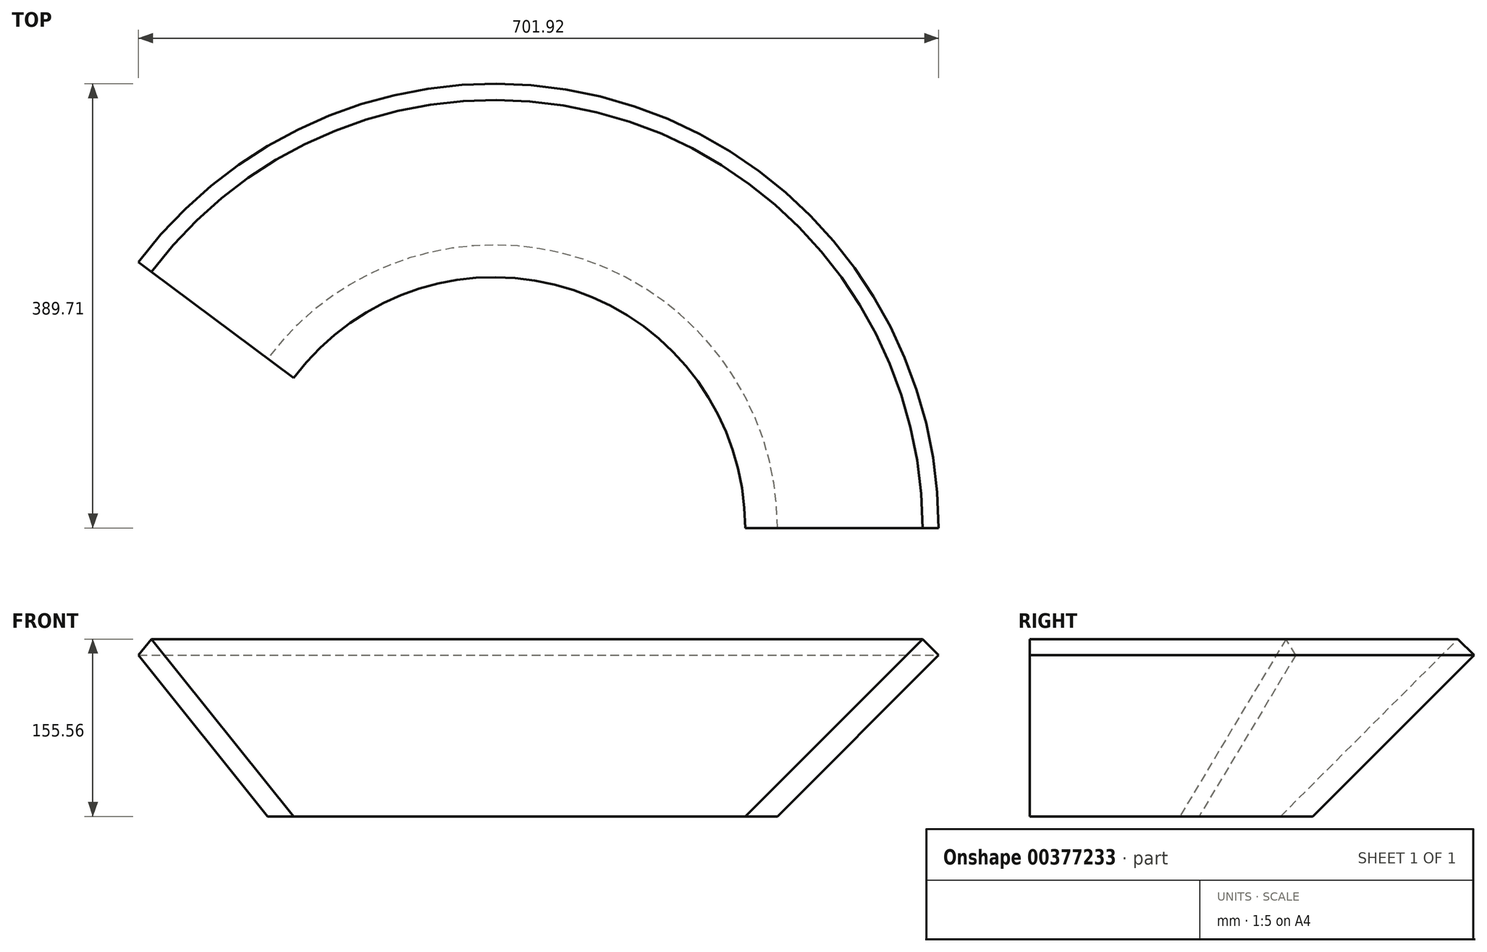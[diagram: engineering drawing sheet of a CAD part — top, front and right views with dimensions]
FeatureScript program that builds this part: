
annotation { "Feature Type Name" : "Feature", "Feature Type Description" : "" }
export const myFeature = defineFeature(function(context is Context, id is Id, definition is map)
    precondition{}
    {
        {
            var Q0;
            Q0=qCreatedBy(makeId("Front.planeOp"),FACE);
            var sketch = newSketch(context, id + "F0", { "sketchPlane" : qUnion([Q0])});
            skLineSegment(sketch, "E0", {"start": v(38.97, 15.56) * mm, "end": v(37.56, 16.97) * mm});
            skLineSegment(sketch, "E1", {"start": v(0, 22) * mm, "end": v(0, 0) * mm, "construction": true});
            skLineSegment(sketch, "E2", {"start": v(37.56, 16.97) * mm, "end": v(22, 1.41) * mm});
            skLineSegment(sketch, "E3", {"start": v(22, 1.41) * mm, "end": v(24.83, 1.41) * mm});
            skLineSegment(sketch, "E4", {"start": v(38.97, 15.56) * mm, "end": v(24.83, 1.41) * mm});
            skSolve(sketch);
        }
        {
            var Q0;
            Q0=makeQuery(id+"F0.imprint","IMPRINT",FACE,{"disambiguationData":[TD([[makeQuery(id+"F0.imprint","IMPRINT",EDGE,{"derivedFrom":sQuery(id+"F0.wireOp",EDGE,"3R4KFfJ1-Y3Kb-D4CS-npq4-7DWoadC4dx8a")}),1.0]])]});
            var Q1;
            Q1=makeQuery(id+"F0.imprint","IMPRINT",FACE,{"disambiguationData":[TD([[makeQuery(id+"F0.imprint","IMPRINT",EDGE,{"derivedFrom":sQuery(id+"F0.wireOp",EDGE,"E0")}),1.0]])]});
            var Q2;
            Q2=sQuery(id+"F0.wireOp",EDGE,"E1");
            revolve(context, id + "F1", {"entities" : qUnion([Q0, Q1]), "axis" : qUnion([Q2]), "revolveType" : RevolveType.ONE_DIRECTION, "oppositeDirection" : true, "angle" : 143.24 * degree, "surfaceOperationType" : NewSurfaceOperationType.NEW});
        }
        {
            var Q0;
            Q0=makeQuery(id+"F1.opRevolve","SWEPT_BODY",BODY,{"disambiguationData":[OSD([sQuery(id+"F0.wireOp",EDGE,"E0"),sQuery(id+"F0.wireOp",EDGE,"E2"),sQuery(id+"F0.wireOp",EDGE,"E3"),sQuery(id+"F0.wireOp",EDGE,"E4")])]});
            var Q1;
            Q1=makeQuery(id+"F1.opRevolve","CAP_VERTEX",VERTEX,{"disambiguationData":[OSD([sQuery(id+"F0.wireOp",EDGE,"E0"),sQuery(id+"F0.wireOp",EDGE,"E2")])],"isStart":true});
            transform(context, id + "F2", {"entities" : qUnion([Q0]), "transformType" : TransformType.SCALE_UNIFORMLY, "scale" : 10, "scalePoint" : qUnion([Q1]), "makeCopy" : false});
        }
    });
